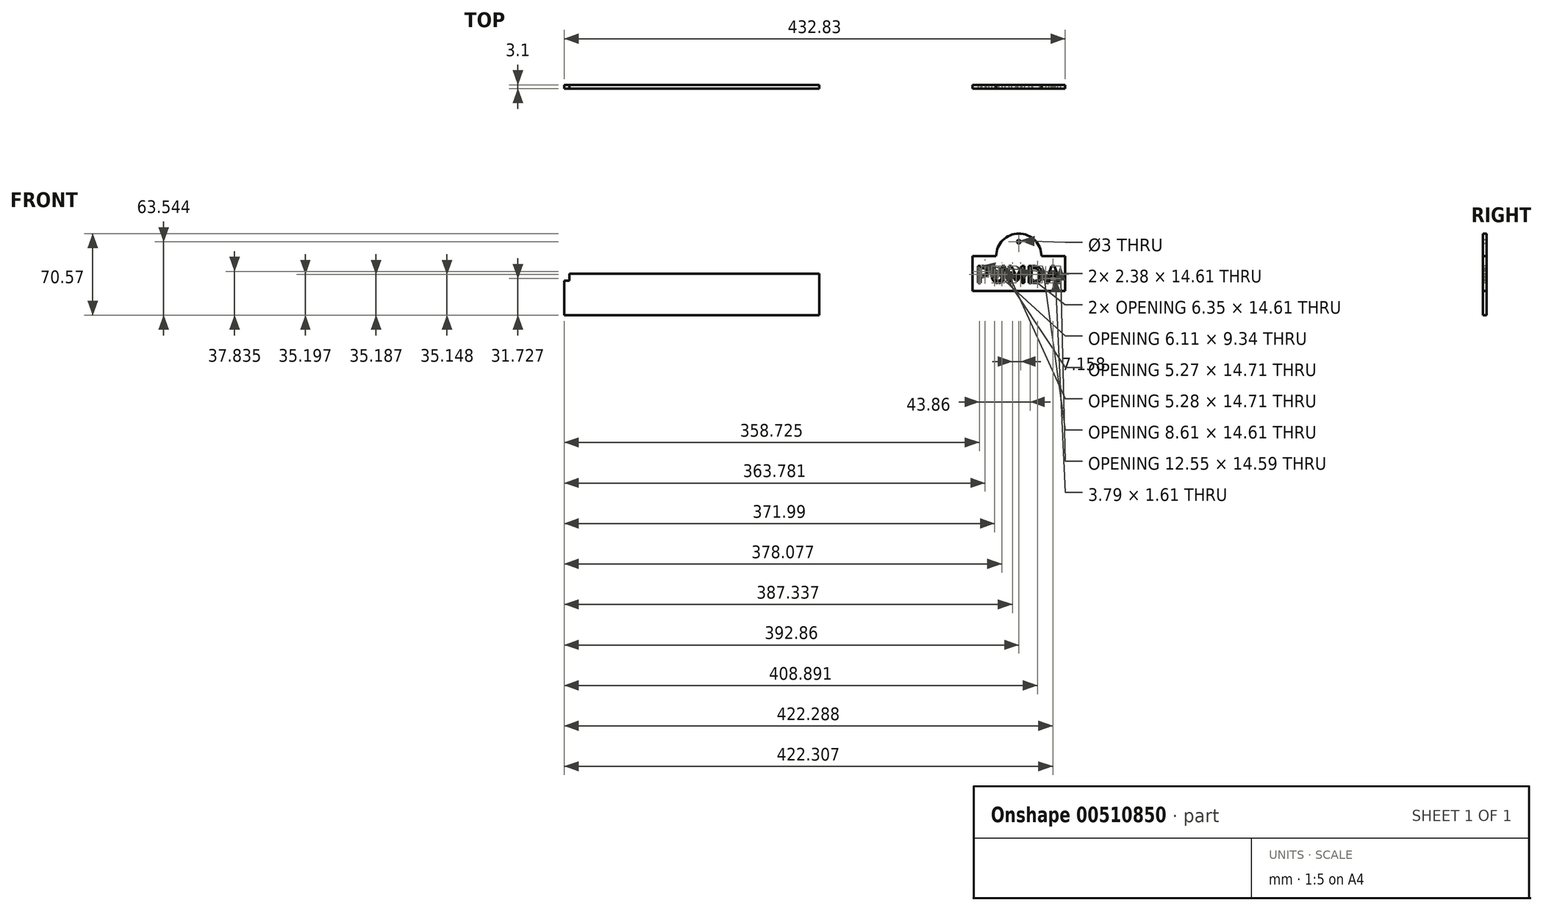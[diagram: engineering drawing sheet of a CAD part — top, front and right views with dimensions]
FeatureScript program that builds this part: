
annotation { "Feature Type Name" : "Feature", "Feature Type Description" : "" }
export const myFeature = defineFeature(function(context is Context, id is Id, definition is map)
    precondition{}
    {
        {
            var Q0;
            Q0=qCreatedBy(makeId("Front.planeOp"),FACE);
            var sketch = newSketch(context, id + "F0", { "sketchPlane" : qUnion([Q0])});
            skLineSegment(sketch, "E0.bottom", {"start": v(-106.65, 4.25) * mm, "end": v(109.17, 4.25) * mm});
            skLineSegment(sketch, "E0.top", {"start": v(-106.65, 10.24) * mm, "end": v(109.17, 10.24) * mm});
            skLineSegment(sketch, "E0.left", {"start": v(-106.65, 4.25) * mm, "end": v(-106.65, 10.24) * mm});
            skLineSegment(sketch, "E0.right", {"start": v(109.17, 4.25) * mm, "end": v(109.17, 10.24) * mm});
            skLineSegment(sketch, "E1.bottom", {"start": v(109.17, 4.25) * mm, "end": v(-111.26, 4.25) * mm});
            skLineSegment(sketch, "E1.top", {"start": v(109.17, -25.73) * mm, "end": v(-111.26, -25.73) * mm});
            skLineSegment(sketch, "E1.left", {"start": v(109.17, 4.25) * mm, "end": v(109.17, -25.73) * mm});
            skLineSegment(sketch, "E1.right", {"start": v(-111.26, 4.25) * mm, "end": v(-111.26, -25.73) * mm});
            skLineSegment(sketch, "E2.bottom", {"start": v(241.57, 25.24) * mm, "end": v(261.97, 25.24) * mm});
            skLineSegment(sketch, "E2.top", {"start": v(241.57, -4.76) * mm, "end": v(321.57, -4.76) * mm});
            skLineSegment(sketch, "E2.left", {"start": v(241.57, 25.24) * mm, "end": v(241.57, -4.76) * mm});
            skLineSegment(sketch, "E2.right", {"start": v(321.57, 25.24) * mm, "end": v(321.57, -4.76) * mm});
            skArc(sketch, "E3", {"start": v(301.17, 25.24) * mm, "mid": v(281.57, 44.84) * mm, "end": v(261.97, 25.24) * mm});
            skCircle(sketch, "E4", {"center": v(281.6, 37.81) * mm, "radius": 1.5 * mm});
            skLineSegment(sketch, "E5.trimOffspring", {"start": v(301.17, 25.24) * mm, "end": v(321.57, 25.24) * mm});
            skText(sketch, "E6", { "text": "PUMDA\n", "fontName": "AllertaStencil-Regular.ttf"});
            const initialGuessF0  = {"E6": [0.24447, 0.00216, 1, 0, 0.01462]};
            skSetInitialGuess(sketch, initialGuessF0);
            skSolve(sketch);
        }
        {
            var Q0;
            Q0=qCreatedBy(makeId("Front.planeOp"),FACE);
            var sketch = newSketch(context, id + "F1", { "sketchPlane" : qUnion([Q0])});
            skSolve(sketch);
        }
        {
            var Q0;
            Q0 = qSketchRegion(id + "F1", true);
            var Q1;
            Q1 = qSketchRegion(id + "F0", true);
            extrude(context, id + "F2", {"entities" : qUnion([Q0, Q1]), "oppositeDirection" : true, "depth" : 3.1 * mm, "offsetDistance" : 25 * mm});
        }
    });
